FCSTD DOCUMENT  (FreeCAD 0.19R24291 (Git))
Label: Problem 07
License: All rights reserved
LicenseURL: http://en.wikipedia.org/wiki/All_rights_reserved
objects: Part::Part2DObjectPython×46, App::FeaturePython×29
note: 46 computed .brp shape members not serialized (recipe doc carries the construction recipe); baked Part::Feature solids carry a one-line shape summary decoded from their .brp

FEATURE [Part::Part2DObjectPython] Circle  # Draft 2D object (typed FeaturePython)
  Area = 0
  FirstAngle = 0
  LastAngle = 0
  MakeFace = false
  Placement = pos=(-41.3406,-5.99158,0) rot=(0,0,1;0rad)
  Radius = 20
FEATURE [Part::Part2DObjectPython] Line  # Draft 2D object (typed FeaturePython)
  Area = 0
  ChamferSize = 0
  Closed = false
  End = (-27.1985,8.15056,0)
  FilletRadius = 0
  Length = 28.2843
  MakeFace = false
  Placement = pos=(-55.4827,8.15056,0) rot=(0,0,1;0rad)
  Points = (2) [(0,0,0),(28.2843,-3.55271e-15,0)]
  Start = (-55.4827,8.15056,0)
  Subdivisions = 0
FEATURE [Part::Part2DObjectPython] Wire  # Draft 2D object (typed FeaturePython)
  Area = 0
  ChamferSize = 0
  Closed = false
  End = (-27.1985,-20.1337,0)
  FilletRadius = 0
  Length = 124.853
  MakeFace = false
  Placement = pos=(-27.1985,8.15056,0) rot=(0,0,1;0rad)
  Points = (5) [(0,0,0),(0,-28.2843,0),(-28.2843,-28.2843,0),(-28.2843,-1.77636e-15,0),(0,-28.2843,0)]
  Start = (-27.1985,8.15056,0)
  Subdivisions = 0
FEATURE [Part::Part2DObjectPython] Line001  # Draft 2D object (typed FeaturePython)
  Area = 0
  ChamferSize = 0
  Closed = false
  End = (-55.4827,-20.1337,0)
  FilletRadius = 0
  Length = 40
  MakeFace = false
  Placement = pos=(-27.1985,8.15056,0) rot=(0,0,1;0rad)
  Points = (2) [(0,0,0),(-28.2843,-28.2843,0)]
  Start = (-27.1985,8.15056,0)
  Subdivisions = 0
FEATURE [Part::Part2DObjectPython] Line003  # Draft 2D object (typed FeaturePython)
  Area = 0
  ChamferSize = 0
  Closed = false
  End = (-21.3406,-5.99158,0)
  FilletRadius = 0
  Length = 40
  MakeFace = false
  Placement = pos=(-61.3406,-5.99158,0) rot=(0,0,1;0rad)
  Points = (2) [(0,0,0),(40,3.55271e-15,0)]
  Start = (-61.3406,-5.99158,0)
  Subdivisions = 0
FEATURE [Part::Part2DObjectPython] Line005  # Draft 2D object (typed FeaturePython)
  Area = 0
  ChamferSize = 0
  Closed = false
  End = (-41.3406,-25.9916,0)
  FilletRadius = 0
  Length = 40
  MakeFace = false
  Placement = pos=(-41.3406,14.0084,0) rot=(0,0,1;0rad)
  Points = (2) [(0,0,0),(0,-40,0)]
  Start = (-41.3406,14.0084,0)
  Subdivisions = 0
FEATURE [Part::Part2DObjectPython] Line006  # Draft 2D object (typed FeaturePython)
  Area = 0
  ChamferSize = 0
  Closed = false
  End = (12.4801,-53.7391,0)
  FilletRadius = 0
  Length = 84.641
  MakeFace = false
  Placement = pos=(18.45,-57.1859,0) rot=(0,0,1;1.0472rad)
  Points = (2) [(2.84217e-14,-77.7476,0),(-3.55271e-14,6.89346,0)]
  Start = (85.7813,-96.0596,0)
  Subdivisions = 0
FEATURE [Part::Part2DObjectPython] Line007  # Draft 2D object (typed FeaturePython)
  Area = 0
  ChamferSize = 0
  Closed = false
  End = (-55.4827,-53.7391,0)
  FilletRadius = 0
  Length = 33.6054
  MakeFace = false
  Placement = pos=(-55.4827,-20.1337,0) rot=(0,0,1;0rad)
  Points = (2) [(0,0,0),(-3.55271e-14,-33.6054,0)]
  Start = (-55.4827,-20.1337,0)
  Subdivisions = 0
FEATURE [Part::Part2DObjectPython] Line008  # Draft 2D object (typed FeaturePython)
  Area = 0
  ChamferSize = 0
  Closed = false
  End = (-27.1985,-53.7391,0)
  FilletRadius = 0
  Length = 33.6054
  MakeFace = false
  Placement = pos=(-27.1985,-20.1337,0) rot=(0,0,1;0rad)
  Points = (2) [(0,0,0),(-7.10543e-15,-33.6054,0)]
  Start = (-27.1985,-20.1337,0)
  Subdivisions = 0
FEATURE [Part::Part2DObjectPython] Line009  # Draft 2D object (typed FeaturePython)
  Area = 0
  ChamferSize = 0
  Closed = false
  End = (-61.3406,-5.99158,0)
  FilletRadius = 0
  Length = 47.7476
  MakeFace = false
  Placement = pos=(-61.3406,-5.99158,0) rot=(0,0,1;0rad)
  Points = (2) [(-7.10543e-15,-47.7476,0),(0,3.55271e-15,0)]
  Start = (-61.3406,-53.7391,0)
  Subdivisions = 0
FEATURE [Part::Part2DObjectPython] Line010  # Draft 2D object (typed FeaturePython)
  Area = 0
  ChamferSize = 0
  Closed = false
  End = (-21.3406,-53.7391,0)
  FilletRadius = 0
  Length = 47.7476
  MakeFace = false
  Placement = pos=(-21.3406,-5.99158,0) rot=(0,0,1;0rad)
  Points = (2) [(0,0,0),(-7.10543e-15,-47.7476,0)]
  Start = (-21.3406,-5.99158,0)
  Subdivisions = 0
FEATURE [Part::Part2DObjectPython] Line011  # Draft 2D object (typed FeaturePython)
  Area = 0
  ChamferSize = 0
  Closed = true
  End = (-41.3406,-25.9916,0)
  FilletRadius = 0
  Length = 0
  MakeFace = false
  Placement = pos=(-41.3406,-25.9916,0) rot=(0,0,1;0rad)
  Points = (2) [(0,0,0),(0,0,0)]
  Start = (-41.3406,-25.9916,0)
  Subdivisions = 0
FEATURE [Part::Part2DObjectPython] Line013  # Draft 2D object (typed FeaturePython)
  Area = 0
  ChamferSize = 0
  Closed = false
  End = (-41.3406,-25.9916,0)
  FilletRadius = 0
  Length = 27.7476
  MakeFace = false
  Placement = pos=(-41.3406,-53.7391,0) rot=(0,0,1;0rad)
  Points = (2) [(0,0,0),(7.10543e-15,27.7476,0)]
  Start = (-41.3406,-53.7391,0)
  Subdivisions = 0
FEATURE [Part::Part2DObjectPython] Line014  # Draft 2D object (typed FeaturePython)
  Area = 0
  ChamferSize = 0
  Closed = false
  End = (85.7813,-96.0596,0)
  FilletRadius = 0
  Length = 51.9615
  MakeFace = false
  Placement = pos=(35.409,-83.3071,0) rot=(0,0,1;1.0472rad)
  Points = (2) [(0,0,0),(14.1421,-50,0)]
  Start = (35.409,-83.3071,0)
  Subdivisions = 0
FEATURE [Part::Part2DObjectPython] Line015  # Draft 2D object (typed FeaturePython)
  Area = 0
  ChamferSize = 0
  Closed = false
  End = (85.7813,-96.0596,0)
  FilletRadius = 0
  Length = 53.8516
  MakeFace = false
  Placement = pos=(32.4801,-88.3801,0) rot=(0,0,1;1.0472rad)
  Points = (2) [(0,0,0),(20,-50,0)]
  Start = (32.4801,-88.3801,0)
  Subdivisions = 0
FEATURE [Part::Part2DObjectPython] Line016  # Draft 2D object (typed FeaturePython)
  Area = 0
  ChamferSize = 0
  Closed = false
  End = (85.7813,-96.0596,0)
  FilletRadius = 0
  Length = 51.9615
  MakeFace = false
  Placement = pos=(49.5511,-58.8122,0) rot=(0,0,1;1.0472rad)
  Points = (2) [(0,0,0),(-14.1421,-50,0)]
  Start = (49.5511,-58.8122,0)
  Subdivisions = 0
FEATURE [Part::Part2DObjectPython] Line017  # Draft 2D object (typed FeaturePython)
  Area = 0
  ChamferSize = 0
  Closed = false
  End = (85.7813,-96.0596,0)
  FilletRadius = 0
  Length = 53.8516
  MakeFace = false
  Placement = pos=(52.4801,-53.7391,0) rot=(0,0,1;1.0472rad)
  Points = (2) [(0,0,0),(-20,-50,0)]
  Start = (52.4801,-53.7391,0)
  Subdivisions = 0
FEATURE [Part::Part2DObjectPython] Line019  # Draft 2D object (typed FeaturePython)
  Area = 0
  ChamferSize = 0
  Closed = false
  End = (-41.3406,14.0084,0)
  FilletRadius = 0
  Length = 83.8207
  MakeFace = false
  Placement = pos=(-41.3406,14.0084,0) rot=(0,0,1;0rad)
  Points = (2) [(83.8207,-7.10543e-15,0),(0,0,0)]
  Start = (42.4801,14.0084,0)
  Subdivisions = 0
FEATURE [Part::Part2DObjectPython] Line020  # Draft 2D object (typed FeaturePython)
  Area = 0
  ChamferSize = 0
  Closed = false
  End = (-41.3406,-25.9916,0)
  FilletRadius = 0
  Length = 83.8207
  MakeFace = false
  Placement = pos=(-41.3406,-25.9916,0) rot=(0,0,1;0rad)
  Points = (2) [(83.8207,7.10543e-15,0),(0,0,0)]
  Start = (42.4801,-25.9916,0)
  Subdivisions = 0
FEATURE [Part::Part2DObjectPython] Line021  # Draft 2D object (typed FeaturePython)
  Area = 0
  ChamferSize = 0
  Closed = false
  End = (-41.3406,-5.99158,0)
  FilletRadius = 0
  Length = 73.8207
  MakeFace = false
  Placement = pos=(-41.3406,-5.99158,0) rot=(0,0,1;0rad)
  Points = (2) [(73.8207,0,0),(0,0,0)]
  Start = (32.4801,-5.99158,0)
  Subdivisions = 0
FEATURE [Part::Part2DObjectPython] Line022  # Draft 2D object (typed FeaturePython)
  Area = 0
  ChamferSize = 0
  Closed = false
  End = (-27.1985,8.15056,0)
  FilletRadius = 0
  Length = 76.7496
  MakeFace = false
  Placement = pos=(-27.1985,8.15056,0) rot=(0,0,1;0rad)
  Points = (2) [(76.7496,-1.77636e-15,0),(-7.10543e-15,0,0)]
  Start = (49.5511,8.15056,0)
  Subdivisions = 0
FEATURE [Part::Part2DObjectPython] Line023  # Draft 2D object (typed FeaturePython)
  Area = 0
  ChamferSize = 0
  Closed = false
  End = (-27.1985,-20.1337,0)
  FilletRadius = 0
  Length = 76.7496
  MakeFace = false
  Placement = pos=(-27.1985,-20.1337,0) rot=(0,0,1;0rad)
  Points = (2) [(76.7496,7.10543e-15,0),(0,0,0)]
  Start = (49.5511,-20.1337,0)
  Subdivisions = 0
FEATURE [Part::Part2DObjectPython] Line024  # Draft 2D object (typed FeaturePython)
  Area = 0
  ChamferSize = 0
  Closed = false
  End = (-41.3406,-103.739,0)
  FilletRadius = 0
  Length = 53.8516
  MakeFace = false
  Placement = pos=(-61.3406,-53.7391,0) rot=(0,0,1;0rad)
  Points = (2) [(0,0,0),(20,-50,0)]
  Start = (-61.3406,-53.7391,0)
  Subdivisions = 0
FEATURE [Part::Part2DObjectPython] Line025  # Draft 2D object (typed FeaturePython)
  Area = 0
  ChamferSize = 0
  Closed = false
  End = (-41.3406,-103.739,0)
  FilletRadius = 0
  Length = 51.9615
  MakeFace = false
  Placement = pos=(-55.4827,-53.7391,0) rot=(0,0,1;0rad)
  Points = (2) [(0,0,0),(14.1421,-50,0)]
  Start = (-55.4827,-53.7391,0)
  Subdivisions = 0
FEATURE [Part::Part2DObjectPython] Line026  # Draft 2D object (typed FeaturePython)
  Area = 0
  ChamferSize = 0
  Closed = false
  End = (-41.3406,-103.739,0)
  FilletRadius = 0
  Length = 50
  MakeFace = false
  Placement = pos=(-41.3406,-25.9916,0) rot=(0,0,1;0rad)
  Points = (2) [(-7.10543e-15,-27.7476,0),(-2.13163e-14,-77.7476,0)]
  Start = (-41.3406,-53.7391,0)
  Subdivisions = 0
FEATURE [Part::Part2DObjectPython] Line027  # Draft 2D object (typed FeaturePython)
  Area = 0
  ChamferSize = 0
  Closed = false
  End = (-41.3406,-103.739,0)
  FilletRadius = 0
  Length = 51.9615
  MakeFace = false
  Placement = pos=(-27.1985,-53.7391,0) rot=(0,0,1;0rad)
  Points = (2) [(0,0,0),(-14.1421,-50,0)]
  Start = (-27.1985,-53.7391,0)
  Subdivisions = 0
FEATURE [Part::Part2DObjectPython] Line028  # Draft 2D object (typed FeaturePython)
  Area = 0
  ChamferSize = 0
  Closed = false
  End = (-41.3406,-103.739,0)
  FilletRadius = 0
  Length = 53.8516
  MakeFace = false
  Placement = pos=(-21.3406,-53.7391,0) rot=(0,0,1;0rad)
  Points = (2) [(0,0,0),(-20,-50,0)]
  Start = (-21.3406,-53.7391,0)
  Subdivisions = 0
FEATURE [Part::Part2DObjectPython] Line029  # Draft 2D object (typed FeaturePython)
  Area = 0
  ChamferSize = 0
  Closed = false
  End = (32.4801,-88.3801,0)
  FilletRadius = 0
  Length = 40
  MakeFace = false
  Placement = pos=(52.4801,-53.7391,0) rot=(0,0,1;0rad)
  Points = (2) [(0,0,0),(-20,-34.641,0)]
  Start = (52.4801,-53.7391,0)
  Subdivisions = 0
FEATURE [Part::Part2DObjectPython] Line030  # Draft 2D object (typed FeaturePython)
  Area = 0
  ChamferSize = 0
  Closed = false
  End = (52.4801,-53.7391,0)
  FilletRadius = 0
  Length = 47.7476
  MakeFace = false
  Placement = pos=(52.4801,-41.4607,0) rot=(0,0,1;0rad)
  Points = (2) [(1.42109e-14,35.4692,0),(-7.10543e-15,-12.2784,0)]
  Start = (52.4801,-5.99158,0)
  Subdivisions = 0
FEATURE [Part::Part2DObjectPython] Line031  # Draft 2D object (typed FeaturePython)
  Area = 0
  ChamferSize = 0
  Closed = false
  End = (32.4801,-88.3801,0)
  FilletRadius = 0
  Length = 82.3886
  MakeFace = false
  Placement = pos=(32.4801,-88.3801,0) rot=(0,0,1;0rad)
  Points = (2) [(1.42109e-14,82.3886,0),(0,0,0)]
  Start = (32.4801,-5.99158,0)
  Subdivisions = 0
FEATURE [Part::Part2DObjectPython] Line032  # Draft 2D object (typed FeaturePython)
  Area = 0
  ChamferSize = 0
  Closed = false
  End = (35.409,-83.3071,0)
  FilletRadius = 0
  Length = 91.4576
  MakeFace = false
  Placement = pos=(35.409,-83.3071,0) rot=(0,0,1;0rad)
  Points = (2) [(-2.13163e-14,91.4576,0),(0,0,0)]
  Start = (35.409,8.15056,0)
  Subdivisions = 0
FEATURE [Part::Part2DObjectPython] Line033  # Draft 2D object (typed FeaturePython)
  Area = 0
  ChamferSize = 0
  Closed = false
  End = (42.4801,-71.0596,0)
  FilletRadius = 0
  Length = 85.0681
  MakeFace = false
  Placement = pos=(42.4801,-71.0596,0) rot=(0,0,1;0rad)
  Points = (2) [(-7.10543e-14,85.0681,0),(0,0,0)]
  Start = (42.4801,14.0084,0)
  Subdivisions = 0
FEATURE [Part::Part2DObjectPython] Line034  # Draft 2D object (typed FeaturePython)
  Area = 0
  ChamferSize = 0
  Closed = false
  End = (49.5511,-58.8122,0)
  FilletRadius = 0
  Length = 66.9627
  MakeFace = false
  Placement = pos=(49.5511,-58.8122,0) rot=(0,0,1;0rad)
  Points = (2) [(9.23706e-14,66.9627,0),(0,0,0)]
  Start = (49.5511,8.15056,0)
  Subdivisions = 0
FEATURE [Part::Part2DObjectPython] Line035  # Draft 2D object (typed FeaturePython)
  Area = 0
  ChamferSize = 0
  Closed = false
  End = (32.4801,-5.99158,0)
  FilletRadius = 0
  Length = 53.3013
  MakeFace = false
  Placement = pos=(32.4801,-5.99158,0) rot=(0,0,1;0rad)
  Points = (2) [(53.3013,-2.4869e-14,0),(0,0,0)]
  Start = (85.7813,-5.99158,0)
  Subdivisions = 0
FEATURE [Part::Part2DObjectPython] Line036  # Draft 2D object (typed FeaturePython)
  Area = 0
  ChamferSize = 0
  Closed = false
  End = (85.7813,-96.0596,0)
  FilletRadius = 0
  Length = 90.0681
  MakeFace = false
  Placement = pos=(85.7813,-96.0596,0) rot=(0,0,1;0rad)
  Points = (2) [(0,90.0681,0),(0,0,0)]
  Start = (85.7813,-5.99158,0)
  Subdivisions = 0
FEATURE [Part::Part2DObjectPython] Line037  # Draft 2D object (typed FeaturePython)
  Area = 0
  ChamferSize = 0
  Closed = false
  End = (85.7813,-5.99158,0)
  FilletRadius = 0
  Length = 47.697
  MakeFace = false
  Placement = pos=(42.4801,14.0084,0) rot=(0,0,1;0rad)
  Points = (2) [(0,0,0),(43.3013,-20,0)]
  Start = (42.4801,14.0084,0)
  Subdivisions = 0
FEATURE [Part::Part2DObjectPython] Line038  # Draft 2D object (typed FeaturePython)
  Area = 0
  ChamferSize = 0
  Closed = false
  End = (85.7813,-5.99158,0)
  FilletRadius = 0
  Length = 52.3199
  MakeFace = false
  Placement = pos=(35.409,8.15056,0) rot=(0,0,1;0rad)
  Points = (2) [(0,0,0),(50.3723,-14.1421,0)]
  Start = (35.409,8.15056,0)
  Subdivisions = 0
FEATURE [Part::Part2DObjectPython] Line039  # Draft 2D object (typed FeaturePython)
  Area = 0
  ChamferSize = 0
  Closed = false
  End = (85.7813,-5.99158,0)
  FilletRadius = 0
  Length = 52.3199
  MakeFace = false
  Placement = pos=(35.409,-20.1337,0) rot=(0,0,1;0rad)
  Points = (2) [(0,0,0),(50.3723,14.1421,0)]
  Start = (35.409,-20.1337,0)
  Subdivisions = 0
FEATURE [Part::Part2DObjectPython] Line040  # Draft 2D object (typed FeaturePython)
  Area = 0
  ChamferSize = 0
  Closed = false
  End = (85.7813,-5.99158,0)
  FilletRadius = 0
  Length = 47.697
  MakeFace = false
  Placement = pos=(42.4801,-25.9916,0) rot=(0,0,1;0rad)
  Points = (2) [(0,0,0),(43.3013,20,0)]
  Start = (42.4801,-25.9916,0)
  Subdivisions = 0
FEATURE [Part::Part2DObjectPython] BSpline  # Draft 2D object (typed FeaturePython)
  Area = 0
  Closed = false
  MakeFace = false
  Parameterization = 1
  Points = (5) [(42.4801,-25.9916,0),(35.409,-20.1337,0),(32.4801,-5.99158,0),(35.409,8.15056,0),(42.4801,14.0084,0)]
FEATURE [Part::Part2DObjectPython] BSpline001  # Draft 2D object (typed FeaturePython)
  Area = 0
  Closed = false
  MakeFace = false
  Parameterization = 1
  Points = (5) [(42.4801,14.0084,0),(49.5511,8.15056,0),(52.4801,-5.99158,0),(49.5511,-20.1337,0),(42.4801,-25.9916,0)]
FEATURE [Part::Part2DObjectPython] Line041  # Draft 2D object (typed FeaturePython)
  Area = 0
  ChamferSize = 0
  Closed = false
  End = (-21.3406,-53.7391,0)
  FilletRadius = 0
  Length = 40
  MakeFace = false
  Placement = pos=(-61.3406,-53.7391,0) rot=(0,0,1;0rad)
  Points = (2) [(0,0,0),(40,1.42109e-14,0)]
  Start = (-61.3406,-53.7391,0)
  Subdivisions = 0
FEATURE [Part::Part2DObjectPython] Line042  # Draft 2D object (typed FeaturePython)
  Area = 0
  ChamferSize = 0
  Closed = false
  End = (-61.3406,-53.7391,0)
  FilletRadius = 0
  Length = 11.6913
  MakeFace = false
  Placement = pos=(-30.71,-53.7675,0) rot=(0,0,1;0rad)
  Points = (2) [(-42.3219,0.0391843,0),(-30.6306,0.0283597,0)]
  Start = (-73.0319,-53.7283,0)
  Subdivisions = 0
FEATURE [Part::Part2DObjectPython] Line043  # Draft 2D object (typed FeaturePython)
  Area = 0
  ChamferSize = 0
  Closed = false
  End = (-21.3406,-53.7391,0)
  FilletRadius = 0
  Length = 115.088
  MakeFace = false
  Placement = pos=(-21.3406,-53.7391,0) rot=(0,0,1;0rad)
  Points = (2) [(115.088,0,0),(0,0,0)]
  Start = (93.7479,-53.7391,0)
  Subdivisions = 0
FEATURE [App::FeaturePython] Dimension  # Draft dimension (typed FeaturePython)
  Diameter = false
  Dimline = (-80.546,-97.675,0)
  Direction = (0,0,0)
  Distance = 50
  End = (-41.3406,-103.739,0)
  Normal = (0,0,1)
  Start = (-41.3406,-53.7391,0)
FEATURE [App::FeaturePython] Dimension001  # Draft dimension (typed FeaturePython)
  Angle = 30
  Center = (12.4801,-53.7391,0)
  Dimline = (24.5875,-56.9089,0)
  FirstAngle = 330
  LastAngle = 360
  Normal = (0,0,1)
FEATURE [App::FeaturePython] Text  # WARN: FeaturePython — macro-defined, semantics opaque (R4)
  Placement = pos=(-66.3851,-7.346,0) rot=(0,0,1;0rad)
  Text = a'
FEATURE [App::FeaturePython] Text001  # WARN: FeaturePython — macro-defined, semantics opaque (R4)
  Placement = pos=(-42.3546,15.6117,0) rot=(0,0,1;0rad)
  Text = d'
FEATURE [App::FeaturePython] Text002  # WARN: FeaturePython — macro-defined, semantics opaque (R4)
  Placement = pos=(-20.6842,-5.41497,0) rot=(0,0,1;0rad)
  Text = c'
FEATURE [App::FeaturePython] Text003  # WARN: FeaturePython — macro-defined, semantics opaque (R4)
  Placement = pos=(-40.6381,-30.5183,0) rot=(0,0,1;0rad)
  Text = b'
FEATURE [App::FeaturePython] Text004  # WARN: FeaturePython — macro-defined, semantics opaque (R4)
  Placement = pos=(-36.347,-9.49158,0) rot=(0,0,1;0rad)
  Text = o'
FEATURE [App::FeaturePython] Text005  # WARN: FeaturePython — macro-defined, semantics opaque (R4)
  Placement = pos=(-47.2895,-51.9741,0) rot=(0,0,1;0rad)
  Text = d(b)
FEATURE [App::FeaturePython] Text006  # WARN: FeaturePython — macro-defined, semantics opaque (R4)
  Placement = pos=(-63.22,-57.5108,0) rot=(0,0,1;0rad)
  Text = a
FEATURE [App::FeaturePython] Text007  # WARN: FeaturePython — macro-defined, semantics opaque (R4)
  Placement = pos=(-40.8527,-107.116,0) rot=(0,0,1;0rad)
  Text = o
FEATURE [App::FeaturePython] Text008  # WARN: FeaturePython — macro-defined, semantics opaque (R4)
  Placement = pos=(-21.3279,-57.7672,0) rot=(0,0,1;0rad)
  Text = b
FEATURE [App::FeaturePython] Text009  # WARN: FeaturePython — macro-defined, semantics opaque (R4)
  Placement = pos=(27.8059,-4.98586,0) rot=(0,0,1;0rad)
  Text = a1'
FEATURE [App::FeaturePython] Text010  # WARN: FeaturePython — macro-defined, semantics opaque (R4)
  Placement = pos=(41.5376,16.0408,0) rot=(0,0,1;0rad)
  Text = d1'
FEATURE [App::FeaturePython] Text011  # WARN: FeaturePython — macro-defined, semantics opaque (R4)
  Placement = pos=(86.8094,-6.05865,0) rot=(0,0,1;0rad)
  Text = o'
FEATURE [App::FeaturePython] Text012  # WARN: FeaturePython — macro-defined, semantics opaque (R4)
  Placement = pos=(53.5529,-5.20041,0) rot=(0,0,1;0rad)
  Text = c1'
FEATURE [App::FeaturePython] Text013  # WARN: FeaturePython — macro-defined, semantics opaque (R4)
  Placement = pos=(42.825,-30.0892,0) rot=(0,0,1;0rad)
  Text = b1'
FEATURE [App::FeaturePython] Text014  # WARN: FeaturePython — macro-defined, semantics opaque (R4)
  Placement = pos=(53.7674,-52.4032,0) rot=(0,0,1;0rad)
  Text = c
FEATURE [App::FeaturePython] Text015  # WARN: FeaturePython — macro-defined, semantics opaque (R4)
  Placement = pos=(29.9515,-92.311,0) rot=(0,0,1;0rad)
  Text = a
FEATURE [App::FeaturePython] Text016  # WARN: FeaturePython — macro-defined, semantics opaque (R4)
  Placement = pos=(86.5948,-98.3186,0) rot=(0,0,1;0rad)
  Text = o
FEATURE [App::FeaturePython] Text017  # WARN: FeaturePython — macro-defined, semantics opaque (R4)
  Placement = pos=(-77.3276,-51.3304,0) rot=(0,0,1;0rad)
  Text = X
FEATURE [App::FeaturePython] Text018  # WARN: FeaturePython — macro-defined, semantics opaque (R4)
  Placement = pos=(90.0277,-50.9013,0) rot=(0,0,1;0rad)
  Text = Y
FEATURE [App::FeaturePython] Text019  # WARN: FeaturePython — macro-defined, semantics opaque (R4)
  Placement = pos=(-72.459,-52.6595,0) rot=(0,0,1;0rad)
  Text = VP
FEATURE [App::FeaturePython] Text020  # WARN: FeaturePython — macro-defined, semantics opaque (R4)
  Placement = pos=(-72.1782,-59.6982,0) rot=(0,0,1;0rad)
  Text = HP
FEATURE [App::FeaturePython] Text021  # WARN: FeaturePython — macro-defined, semantics opaque (R4)
  Placement = pos=(-89.9865,2.30912,0) rot=(0,0,1;0rad)
  Text = I
FEATURE [App::FeaturePython] Text024  # WARN: FeaturePython — macro-defined, semantics opaque (R4)
  Placement = pos=(97.5373,8.74586,0) rot=(0,0,1;0rad)
  Text = IV
FEATURE [App::FeaturePython] Text025  # WARN: FeaturePython — macro-defined, semantics opaque (R4)
  Placement = pos=(-32.3611,-114.524,0) rot=(0,0,1;0rad)
  Text = ALL DIMENSIONS ARE IN mm
FEATURE [App::FeaturePython] Text026  # WARN: FeaturePython — macro-defined, semantics opaque (R4)
  Placement = pos=(-90.8014,-70.8337,0) rot=(0,0,1;0rad)
  Text = II
FEATURE [App::FeaturePython] Text027  # WARN: FeaturePython — macro-defined, semantics opaque (R4)
  Placement = pos=(98.6179,-69.2958,0) rot=(0,0,1;0rad)
  Text = III
FEATURE [Part::Part2DObjectPython] Line044  # Draft 2D object (typed FeaturePython)
  Area = 0
  ChamferSize = 0
  Closed = false
  End = (-58.7616,5.54915,0)
  FilletRadius = 0
  Length = 9.81401
  MakeFace = false
  Placement = pos=(-65.1695,12.9824,0) rot=(0,0,1;0rad)
  Points = (2) [(0,0,0),(6.40795,-7.43323,0)]
  Start = (-65.1695,12.9824,0)
  Subdivisions = 0
FEATURE [Part::Part2DObjectPython] Line045  # Draft 2D object (typed FeaturePython)
  Area = 0
  ChamferSize = 0
  Closed = false
  End = (-72.8591,12.9824,0)
  FilletRadius = 0
  Length = 7.68954
  MakeFace = false
  Placement = pos=(-60.8121,12.9824,0) rot=(0,0,1;0rad)
  Points = (2) [(-4.35741,0,0),(-12.047,-1.77636e-15,0)]
  Start = (-65.1695,12.9824,0)
  Subdivisions = 0
FEATURE [App::FeaturePython] Text028  # WARN: FeaturePython — macro-defined, semantics opaque (R4)
  Placement = pos=(-83.6244,11.1882,0) rot=(0,0,1;0rad)
  Text = R 20
